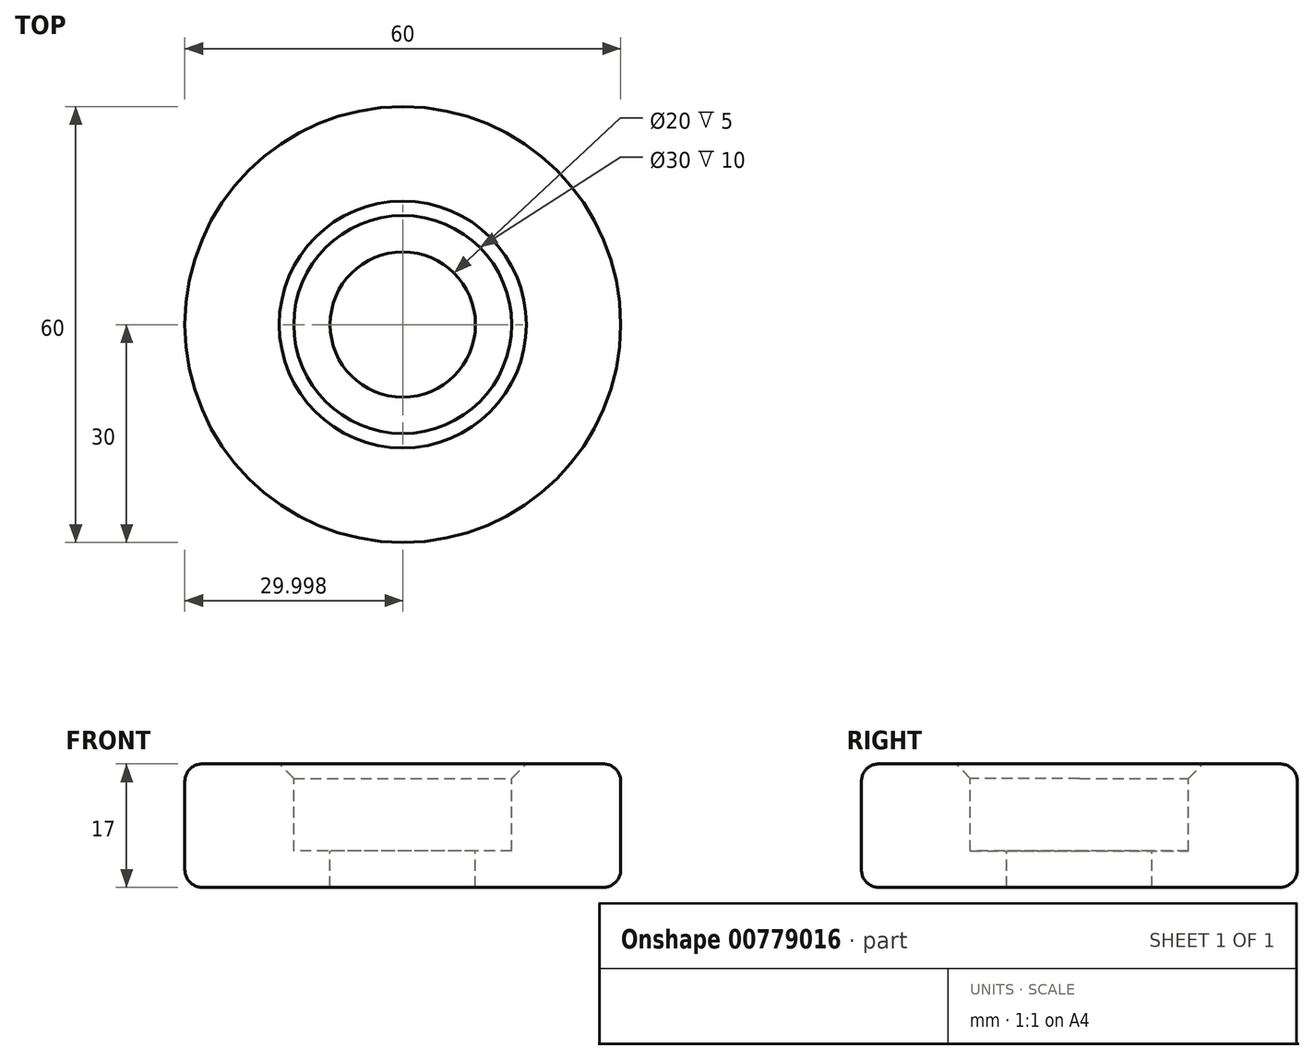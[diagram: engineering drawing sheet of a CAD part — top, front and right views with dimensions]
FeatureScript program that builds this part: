
annotation { "Feature Type Name" : "Feature", "Feature Type Description" : "" }
export const myFeature = defineFeature(function(context is Context, id is Id, definition is map)
    precondition{}
    {
        {
            var Q0;
            Q0=qCreatedBy(makeId("Front.planeOp"),FACE);
            var sketch = newSketch(context, id + "F0", { "sketchPlane" : qUnion([Q0])});
            skLineSegment(sketch, "E0", {"start": v(10.54, 17.75) * mm, "end": v(10.54, 12.75) * mm});
            skLineSegment(sketch, "E1", {"start": v(10.54, 12.75) * mm, "end": v(30.54, 12.75) * mm});
            skLineSegment(sketch, "E2", {"start": v(30.54, 12.75) * mm, "end": v(30.54, 29.75) * mm});
            skLineSegment(sketch, "E3", {"start": v(30.54, 29.75) * mm, "end": v(15.54, 29.75) * mm});
            skLineSegment(sketch, "E4", {"start": v(15.54, 29.75) * mm, "end": v(15.54, 17.75) * mm});
            skLineSegment(sketch, "E5", {"start": v(15.54, 17.75) * mm, "end": v(10.54, 17.75) * mm});
            skLineSegment(sketch, "E6", {"start": v(0.54, 40.98) * mm, "end": v(0.54, 4.04) * mm, "construction": true});
            skLineSegment(sketch, "E7", {"start": v(10.54, 12.75) * mm, "end": v(0.54, 12.75) * mm, "construction": true});
            skLineSegment(sketch, "E8", {"start": v(15.54, 17.75) * mm, "end": v(0.54, 17.75) * mm});
            skSolve(sketch);
        }
        {
            var Q0;
            Q0=makeQuery(id+"F0.imprint","IMPRINT",FACE,{"disambiguationData":[TD([[makeQuery(id+"F0.imprint","IMPRINT",EDGE,{"derivedFrom":sQuery(id+"F0.wireOp",EDGE,"E0")}),1.0]])]});
            var Q1;
            Q1=sQuery(id+"F0.wireOp",EDGE,"E6");
            revolve(context, id + "F1", {"surfaceOperationType" : NewSurfaceOperationType.NEW, "entities" : qUnion([Q0]), "axis" : qUnion([Q1]), "revolveType" : RevolveType.FULL});
        }
        {
            var Q0;
            Q0=makeQuery(id+"F1.opRevolve","SWEPT_EDGE",EDGE,{"disambiguationData":[OSD([sQuery(id+"F0.wireOp",EDGE,"E2"),sQuery(id+"F0.wireOp",EDGE,"E3")])]});
            var Q1;
            Q1=makeQuery(id+"F1.opRevolve","SWEPT_EDGE",EDGE,{"disambiguationData":[OSD([sQuery(id+"F0.wireOp",EDGE,"E1"),sQuery(id+"F0.wireOp",EDGE,"E2")])]});
            fillet(context, id + "F2", {"entities" : qUnion([Q0, Q1]), "radius" : 2.4 * mm, "tangentPropagation" : true, "allowEdgeOverflow" : false});
        }
        {
            var Q0;
            Q0=makeQuery(id+"F1.opRevolve","SWEPT_EDGE",EDGE,{"disambiguationData":[OSD([sQuery(id+"F0.wireOp",EDGE,"E3"),sQuery(id+"F0.wireOp",EDGE,"E4")])]});
            chamfer(context, id + "F3", {"entities" : qUnion([Q0]), "width" : 2 * mm, "tangentPropagation" : true});
        }
    });
